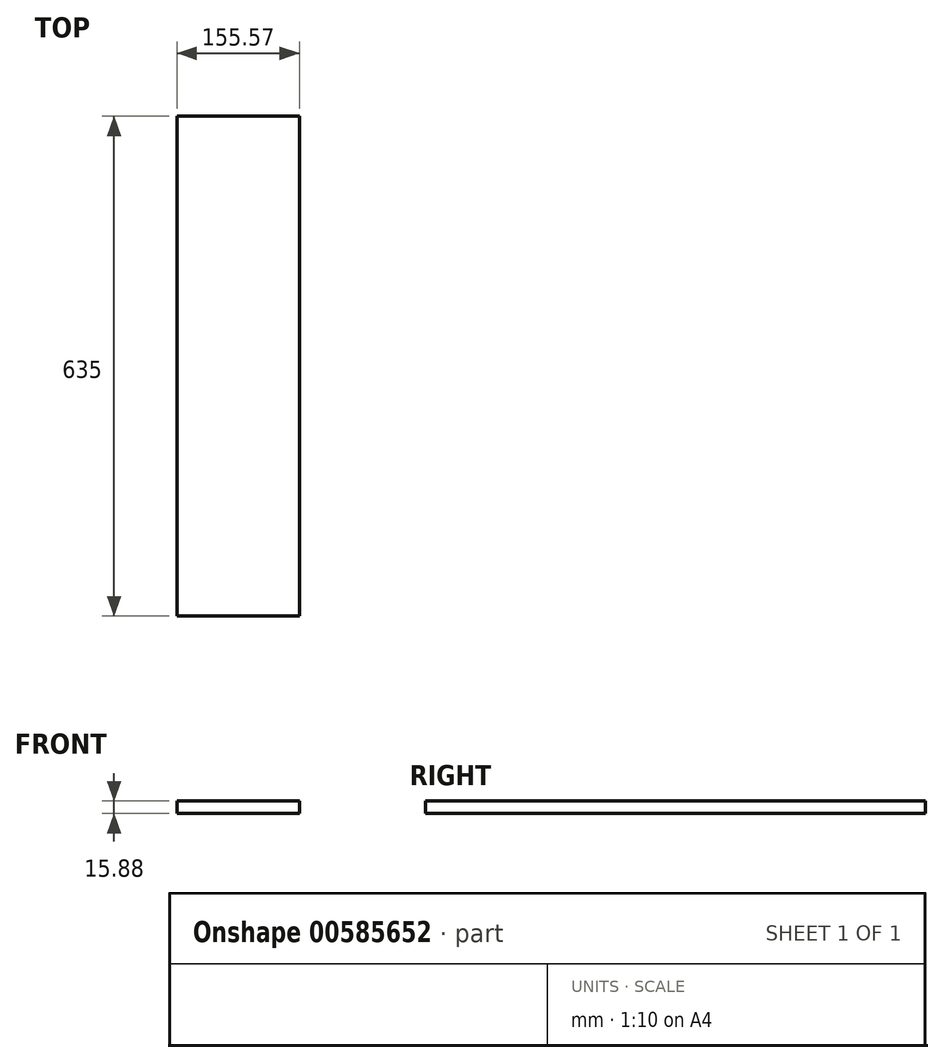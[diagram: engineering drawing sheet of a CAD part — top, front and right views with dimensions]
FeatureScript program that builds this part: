
annotation { "Feature Type Name" : "Feature", "Feature Type Description" : "" }
export const myFeature = defineFeature(function(context is Context, id is Id, definition is map)
    precondition{}
    {
        {
            var Q0;
            Q0=qCreatedBy(makeId("Front.planeOp"),FACE);
            var sketch = newSketch(context, id + "F0", { "sketchPlane" : qUnion([Q0])});
            skLineSegment(sketch, "E0.bottom", {"start": v(0, 0) * mm, "end": v(155.58, 0) * mm});
            skLineSegment(sketch, "E0.top", {"start": v(0, 15.88) * mm, "end": v(155.58, 15.88) * mm});
            skLineSegment(sketch, "E0.left", {"start": v(0, 0) * mm, "end": v(0, 15.88) * mm});
            skLineSegment(sketch, "E0.right", {"start": v(155.58, 0) * mm, "end": v(155.58, 15.88) * mm});
            skSolve(sketch);
        }
        {
            var Q0;
            Q0=makeQuery(id+"F0.imprint","IMPRINT",FACE,{"disambiguationData":[TD([[makeQuery(id+"F0.imprint","IMPRINT",EDGE,{"derivedFrom":sQuery(id+"F0.wireOp",EDGE,"E0.bottom")}),1.0]])]});
            extrude(context, id + "F1", {"entities" : qUnion([Q0]), "oppositeDirection" : true, "depth" : 635 * mm, "offsetDistance" : 25.4 * mm});
        }
    });
